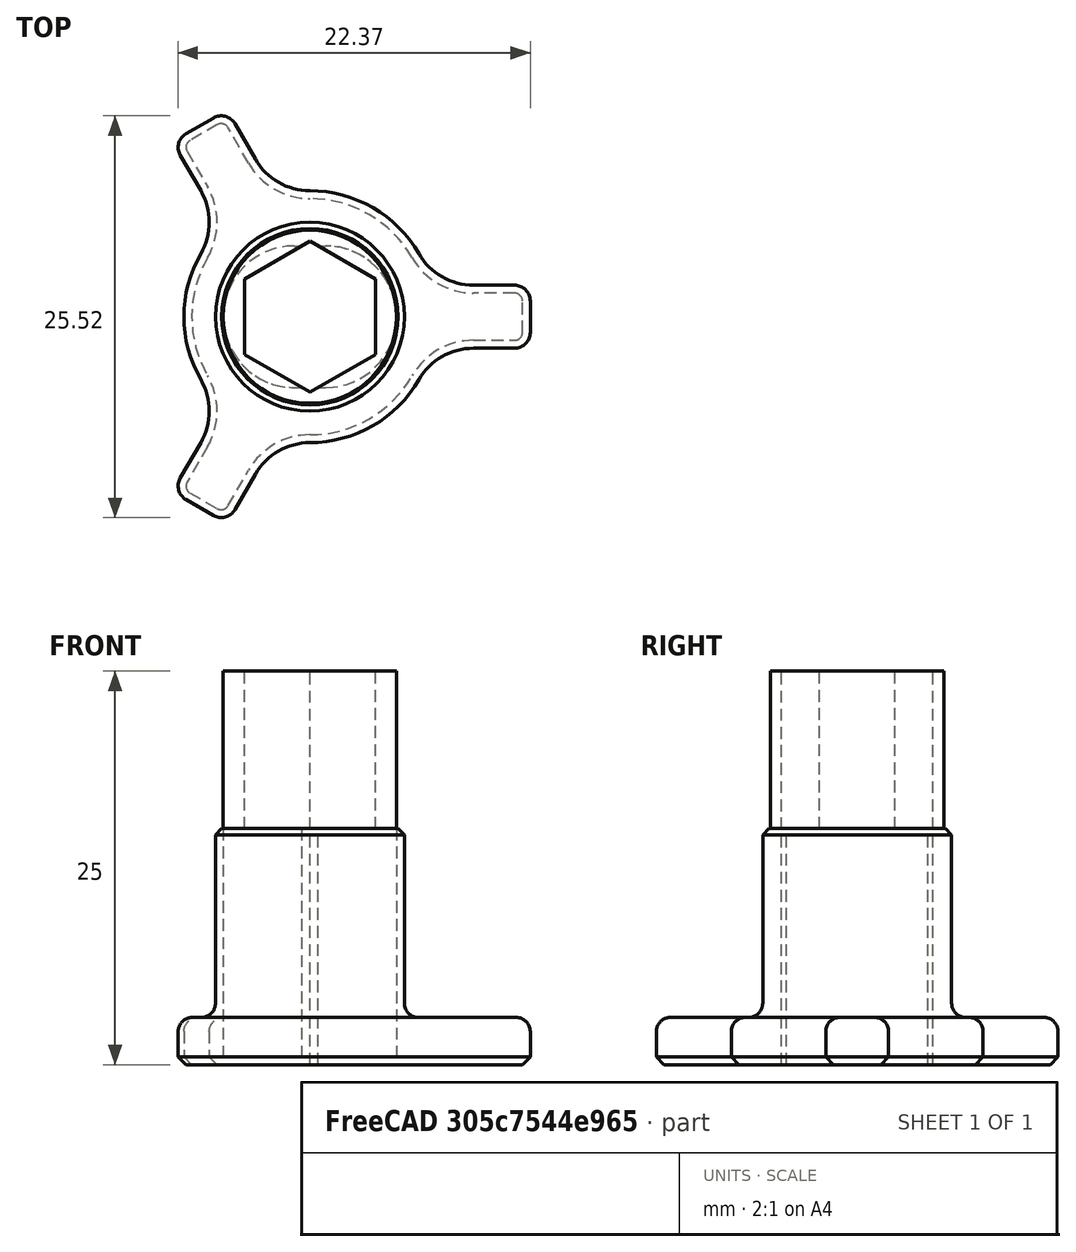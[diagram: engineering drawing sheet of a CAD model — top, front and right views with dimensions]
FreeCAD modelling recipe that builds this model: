
FCSTD DOCUMENT  (FreeCAD 0.19R22366 (Git))
Label: festo key 3
License: All rights reserved
LicenseURL: http://en.wikipedia.org/wiki/All_rights_reserved
objects: Sketcher::SketchObject×5, PartDesign::Pad×3, PartDesign::Pocket×2, PartDesign::Chamfer×2, PartDesign::PolarPattern×1, PartDesign::Fillet×1, PartDesign::Body×1, Mesh::Feature×1
note: 23 computed .brp shape members not serialized (recipe doc carries the construction recipe); baked Part::Feature solids carry a one-line shape summary decoded from their .brp

FEATURE [Sketcher::SketchObject] Sketch
  MapMode = 5
  Support = -> [XY_Plane]
  sketch-geometry (8):
    g0: LineSegment StartX=14 StartY=1 StartZ=0 EndX=14 EndY=-1 EndZ=0
    g1: ArcOfCircle CenterX=13 CenterY=1 CenterZ=0 NormalX=0 NormalY=0 NormalZ=1 AngleXU=0 Radius=1 StartAngle=0 EndAngle=1.5708
    g2: ArcOfCircle CenterX=13 CenterY=-1 CenterZ=0 NormalX=0 NormalY=0 NormalZ=1 AngleXU=0 Radius=1 StartAngle=4.71239 EndAngle=6.28319
    g3: LineSegment StartX=13 StartY=2 StartZ=0 EndX=10.3923 EndY=2 EndZ=0
    g4: LineSegment StartX=13 StartY=-2 StartZ=0 EndX=10.3923 EndY=-2 EndZ=0
    g5: ArcOfCircle CenterX=10.3923 CenterY=6 CenterZ=0 NormalX=0 NormalY=0 NormalZ=1 AngleXU=0 Radius=4 StartAngle=3.66519 EndAngle=4.71239
    g6: ArcOfCircle CenterX=10.3923 CenterY=-6 CenterZ=0 NormalX=0 NormalY=0 NormalZ=1 AngleXU=0 Radius=4 StartAngle=1.5708 EndAngle=2.61799
    g7: ArcOfCircle CenterX=0 CenterY=0 CenterZ=0 NormalX=0 NormalY=0 NormalZ=1 AngleXU=0 Radius=8 StartAngle=0.523599 EndAngle=5.75959
  constraints (22):
    c: DistanceX(g-1,g0) = 14
    c: Symmetric(g0,g0,g-1)
    c: DistanceY(g0,g0) = 2
    c: Coincident(g1,g0)
    c: Coincident(g2,g0)
    c: Horizontal(g2,g0)
    c: Radius(g1) = 1
    c: Horizontal(g3)
    c: Tangent(g3,g1) = -1.5708
    c: Coincident(g4,g2)
    c: Horizontal(g4)
    c: Equal(g3,g4)
    c: Tangent(g5,g3) = 1.5708
    c: Horizontal(g1,g0)
    c: Equal(g2,g1)
    c: Equal(g5,g6)
    c: Coincident(g7,g-1)
    c: Radius(g7) = 8
    c: Tangent(g7,g5) = 1.5708
    c: Tangent(g6,g4) = -1.5708
    c: Tangent(g7,g6) = 1.5708
    c: DistanceY(g6,g7) = 6
FEATURE [PartDesign::Pad] Pad
  Length = 3
  Length2 = 100
  Profile = -> Sketch
  Refine = true
  Type = 0
FEATURE [Sketcher::SketchObject] Sketch001
  MapMode = 5
  Support = -> [XY_Plane]
  sketch-geometry (4):
    g0: ArcOfCircle CenterX=-1 CenterY=0 CenterZ=0 NormalX=0 NormalY=0 NormalZ=1 AngleXU=0 Radius=4.5 StartAngle=1.5708 EndAngle=4.71239
    g1: ArcOfCircle CenterX=1 CenterY=0 CenterZ=0 NormalX=0 NormalY=0 NormalZ=1 AngleXU=0 Radius=4.5 StartAngle=4.71239 EndAngle=7.85398
    g2: LineSegment StartX=-1 StartY=-4.5 StartZ=0 EndX=1 EndY=-4.5 EndZ=0
    g3: LineSegment StartX=-1 StartY=4.5 StartZ=0 EndX=1 EndY=4.5 EndZ=0
  constraints (9):
    c: Tangent(g0,g3)
    c: Tangent(g0,g2)
    c: Tangent(g2,g1)
    c: Tangent(g3,g1)
    c: Horizontal(g2)
    c: Equal(g0,g1)
    c: DistanceX(g0,g1) = 2
    c: Radius(g1) = 4.5
    c: Symmetric(g0,g1,g-1)
FEATURE [PartDesign::PolarPattern] PolarPattern
  Angle = 360
  Axis = -> Sketch [N_Axis]
  BaseFeature = -> Pad
  Occurrences = 3
  Originals = -> [Pad]
  Refine = true
FEATURE [Sketcher::SketchObject] Sketch002
  AttachmentOffset = pos=(0,0,3) rot=(0,0,1;0rad)
  MapMode = 5
  Placement = pos=(0,0,3) rot=(0,0,1;0rad)
  Support = -> [XY_Plane]
  sketch-geometry (1):
    g0: Circle CenterX=0 CenterY=0 CenterZ=0 NormalX=0 NormalY=0 NormalZ=1 AngleXU=0 Radius=6
  constraints (2):
    c: Coincident(g0,g-1)
    c: Radius(g0) = 6
FEATURE [PartDesign::Pad] Pad001
  BaseFeature = -> PolarPattern
  Length = 12
  Length2 = 100
  Profile = -> Sketch002
  Refine = true
  Type = 0
FEATURE [PartDesign::Pocket] Pocket
  BaseFeature = -> Pad001
  Length = 5
  Length2 = 100
  Profile = -> Sketch001
  Refine = true
  Reversed = true
  Type = 1
FEATURE [Sketcher::SketchObject] Sketch003
  AttachmentOffset = pos=(0,0,15) rot=(0,0,1;0rad)
  MapMode = 5
  Placement = pos=(0,0,15) rot=(0,0,1;0rad)
  Support = -> [XY_Plane]
  sketch-geometry (1):
    g0: Circle CenterX=0 CenterY=0 CenterZ=0 NormalX=0 NormalY=0 NormalZ=1 AngleXU=0 Radius=5.5
  constraints (2):
    c: Coincident(g0,g-1)
    c: Radius(g0) = 5.5
FEATURE [PartDesign::Pad] Pad002
  BaseFeature = -> Pocket
  Length = 10
  Length2 = 100
  Profile = -> Sketch003
  Refine = true
  Type = 0
FEATURE [Sketcher::SketchObject] Sketch004
  MapMode = 5
  Support = -> [XY_Plane]
  sketch-geometry (7):
    g0: LineSegment StartX=4.15692 StartY=-2.4 StartZ=0 EndX=4.15692 EndY=2.4 EndZ=0
    g1: LineSegment StartX=4.15692 StartY=2.4 StartZ=0 EndX=0 EndY=4.8 EndZ=0
    g2: LineSegment StartX=0 StartY=4.8 StartZ=0 EndX=-4.15692 EndY=2.4 EndZ=0
    g3: LineSegment StartX=-4.15692 StartY=2.4 StartZ=0 EndX=-4.15692 EndY=-2.4 EndZ=0
    g4: LineSegment StartX=-4.15692 StartY=-2.4 StartZ=0 EndX=0 EndY=-4.8 EndZ=0
    g5: LineSegment StartX=0 StartY=-4.8 StartZ=0 EndX=4.15692 EndY=-2.4 EndZ=0
    g6: Circle [constr] CenterX=0 CenterY=0 CenterZ=0 NormalX=0 NormalY=0 NormalZ=1 AngleXU=0 Radius=4.8
  constraints (16):
    c: Coincident(g0,g1)
    c: Coincident(g1,g2)
    c: Coincident(g2,g3)
    c: Coincident(g3,g4)
    c: Coincident(g4,g5)
    c: Coincident(g5,g0)
    c: Equal(g0, g1-g5) x5
    c: PointOnObject(g0,g6)
    c: PointOnObject(g1,g6)
    c: PointOnObject(g2,g6)
    c: PointOnObject(g3,g6)
    c: PointOnObject(g4,g6)
    c: PointOnObject(g5,g6)
    c: Coincident(g6,g-1)
    c: Vertical(g0)
    c: Radius(g6) = 4.8
FEATURE [PartDesign::Pocket] Pocket001
  BaseFeature = -> Pad002
  Length = 5
  Length2 = 100
  Profile = -> Sketch004
  Refine = true
  Reversed = true
  Type = 1
FEATURE [PartDesign::Fillet] Fillet
  Base = -> Pocket001 [Face4]
  BaseFeature = -> Pocket001
  Radius = 0.9
  Refine = true
  SupportTransform = false
FEATURE [PartDesign::Chamfer] Chamfer
  Angle = 45
  Base = -> Fillet [Edge170]
  BaseFeature = -> Fillet
  ChamferType = 0
  FlipDirection = false
  Refine = true
  Size = 0.4
  Size2 = 1
  SupportTransform = false
FEATURE [PartDesign::Chamfer] Chamfer001
  Angle = 45
  Base = -> Chamfer [Edge104]
  BaseFeature = -> Chamfer
  ChamferType = 0
  FlipDirection = false
  Refine = true
  Size = 0.5
  Size2 = 1
  SupportTransform = false
FEATURE [PartDesign::Body] Body
  Group = -> [Sketch,Pad,Sketch001,PolarPattern,Sketch002,Pad001,Pocket,Sketch003,Pad002,Sketch004,Pocket001,Fillet,Chamfer,Chamfer001]
  Origin = -> Origin
  Tip = -> Chamfer001
FEATURE [Mesh::Feature] Mesh  label="Chamfer001 (Meshed)"
